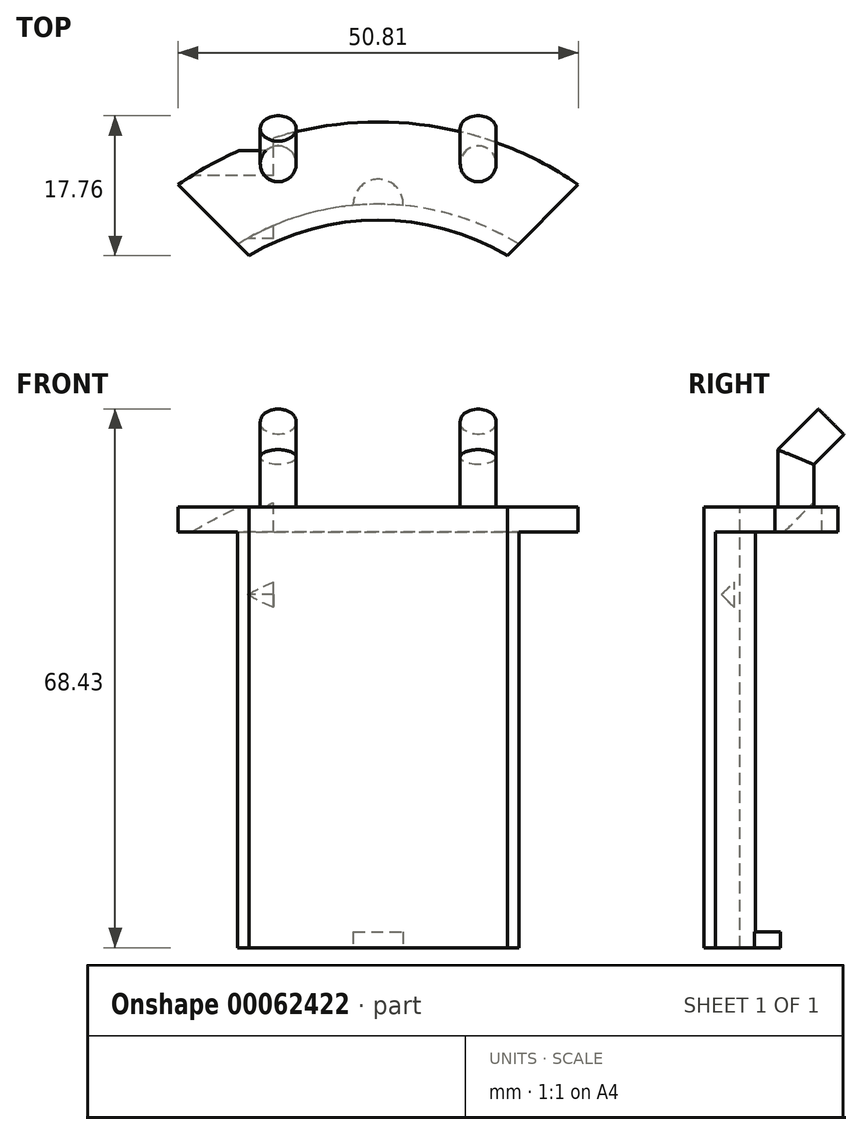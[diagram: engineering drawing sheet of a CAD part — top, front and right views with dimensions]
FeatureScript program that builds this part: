
annotation { "Feature Type Name" : "Feature", "Feature Type Description" : "" }
export const myFeature = defineFeature(function(context is Context, id is Id, definition is map)
    precondition{}
    {
        {
            var Q0;
            Q0=qCreatedBy(makeId("Top.planeOp"),FACE);
            var sketch = newSketch(context, id + "F0", { "sketchPlane" : qUnion([Q0])});
            skLineSegment(sketch, "E0.bottom", {"start": v(0, 0) * mm, "end": v(31.75, 0) * mm});
            skLineSegment(sketch, "E0.top", {"start": v(0, 9.52) * mm, "end": v(31.75, 9.52) * mm});
            skLineSegment(sketch, "E0.left", {"start": v(0, 0) * mm, "end": v(0, 9.52) * mm});
            skLineSegment(sketch, "E0.right", {"start": v(31.75, 0) * mm, "end": v(31.75, 9.52) * mm});
            skSolve(sketch);
        }
        {
            var Q0;
            Q0=makeQuery(id+"F0.imprint","IMPRINT",FACE,{"disambiguationData":[TD([[makeQuery(id+"F0.imprint","IMPRINT",EDGE,{"derivedFrom":sQuery(id+"F0.wireOp",EDGE,"E0.bottom")}),1.0]])]});
            extrude(context, id + "F1", {"entities" : qUnion([Q0]), "depth" : 3.17 * mm});
        }
        {
            var Q0;
            Q0=makeQuery(id+"F1.opExtrude","SWEPT_FACE",FACE,{"disambiguationData":[OSD([sQuery(id+"F0.wireOp",EDGE,"E0.right")])]});
            cPlane(context, id + "F2", {"entities" : qUnion([Q0]), "cplaneType" : CPlaneType.OFFSET, "offset" : 3.17 * mm, "oppositeDirection" : true, "width" : 152.4 * mm, "height" : 152.4 * mm});
        }
        {
            var Q0;
            Q0=qCreatedBy(id+"F2.planeOp",FACE);
            var sketch = newSketch(context, id + "F3", { "sketchPlane" : qUnion([Q0])});
            skLineSegment(sketch, "E1", {"start": v(7.14, 3.18) * mm, "end": v(7.14, 9.53) * mm});
            skLineSegment(sketch, "E2", {"start": v(7.14, 9.53) * mm, "end": v(11.63, 14.02) * mm});
            skSolve(sketch);
        }
        {
            var Q0;
            Q0=makeQuery(id+"F1.opExtrude","CAP_FACE",FACE,{"disambiguationData":[OSD([sQuery(id+"F0.wireOp",EDGE,"E0.bottom"),sQuery(id+"F0.wireOp",EDGE,"E0.top"),sQuery(id+"F0.wireOp",EDGE,"E0.left"),sQuery(id+"F0.wireOp",EDGE,"E0.right")])],"isStart":false});
            var sketch = newSketch(context, id + "F4", { "sketchPlane" : qUnion([Q0])});
            skCircle(sketch, "E3", {"center": v(28.57, 7.14) * mm, "radius": 2.29 * mm});
            skSolve(sketch);
        }
        {
            var Q0;
            Q0=makeQuery(id+"F4.imprint","IMPRINT",FACE,{"disambiguationData":[TD([[makeQuery(id+"F4.imprint","IMPRINT",EDGE,{"derivedFrom":sQuery(id+"F4.wireOp",EDGE,"E3")}),1.0]])]});
            var Q1;
            Q1=sQuery(id+"F3.wireOp",EDGE,"E1");
            var Q2;
            Q2=sQuery(id+"F3.wireOp",EDGE,"E2");
            sweep(context, id + "F5", {"operationType" : NewBodyOperationType.ADD, "profiles" : qUnion([Q0]), "path" : qUnion([Q1, Q2])});
        }
        {
            var Q0;
            Q0=qCreatedBy(id+"F2.planeOp",FACE);
            cPlane(context, id + "F6", {"entities" : qUnion([Q0]), "cplaneType" : CPlaneType.OFFSET, "offset" : 25.4 * mm, "oppositeDirection" : true, "width" : 152.4 * mm, "height" : 152.4 * mm});
        }
        {
            var Q0;
            Q0=qCreatedBy(id+"F6.planeOp",FACE);
            var sketch = newSketch(context, id + "F7", { "sketchPlane" : qUnion([Q0])});
            skLineSegment(sketch, "E4.0", {"start": v(7.14, 3.18) * mm, "end": v(7.14, 9.53) * mm});
            skLineSegment(sketch, "E4.1", {"start": v(7.14, 9.53) * mm, "end": v(11.63, 14.02) * mm});
            skSolve(sketch);
        }
        {
            var Q0;
            Q0=makeQuery(id+"F1.opExtrude","CAP_FACE",FACE,{"disambiguationData":[OSD([sQuery(id+"F0.wireOp",EDGE,"E0.bottom"),sQuery(id+"F0.wireOp",EDGE,"E0.top"),sQuery(id+"F0.wireOp",EDGE,"E0.left"),sQuery(id+"F0.wireOp",EDGE,"E0.right")])],"isStart":false});
            var sketch = newSketch(context, id + "F8", { "sketchPlane" : qUnion([Q0])});
            skCircle(sketch, "E5", {"center": v(3.17, 7.14) * mm, "radius": 2.29 * mm});
            skSolve(sketch);
        }
        {
            var Q0;
            Q0=makeQuery(id+"F8.imprint","IMPRINT",FACE,{"disambiguationData":[TD([[makeQuery(id+"F8.imprint","IMPRINT",EDGE,{"derivedFrom":sQuery(id+"F8.wireOp",EDGE,"E5")}),1.0]])]});
            var Q1;
            Q1=sQuery(id+"F7.wireOp",EDGE,"E4.0");
            var Q2;
            Q2=sQuery(id+"F7.wireOp",EDGE,"E4.1");
            sweep(context, id + "F9", {"operationType" : NewBodyOperationType.ADD, "profiles" : qUnion([Q0]), "path" : qUnion([Q1, Q2])});
        }
        {
            var Q0;
            Q0=makeQuery(id+"F1.opExtrude","CAP_FACE",FACE,{"disambiguationData":[OSD([sQuery(id+"F0.wireOp",EDGE,"E0.bottom"),sQuery(id+"F0.wireOp",EDGE,"E0.top"),sQuery(id+"F0.wireOp",EDGE,"E0.left"),sQuery(id+"F0.wireOp",EDGE,"E0.right")])],"isStart":false});
            var sketch = newSketch(context, id + "F10", { "sketchPlane" : qUnion([Q0])});
            skArc(sketch, "E6", {"start": v(41.28, 4.48) * mm, "mid": v(15.88, 12.46) * mm, "end": v(-9.52, 4.48) * mm});
            skArc(sketch, "E7", {"start": v(32.27, -4.52) * mm, "mid": v(15.88, 0) * mm, "end": v(-0.52, -4.52) * mm});
            skLineSegment(sketch, "E8", {"start": v(-9.53, 4.48) * mm, "end": v(-0.52, -4.52) * mm});
            skLineSegment(sketch, "E9", {"start": v(32.27, -4.52) * mm, "end": v(41.27, 4.48) * mm});
            skSolve(sketch);
        }
        {
            var Q0;
            Q0 = qSketchRegion(id + "F10", true);
            var Q1;
            Q1=makeQuery(id+"F1.opExtrude","CAP_FACE",FACE,{"disambiguationData":[OSD([sQuery(id+"F0.wireOp",EDGE,"E0.bottom"),sQuery(id+"F0.wireOp",EDGE,"E0.top"),sQuery(id+"F0.wireOp",EDGE,"E0.left"),sQuery(id+"F0.wireOp",EDGE,"E0.right")])],"isStart":true});
            extrude(context, id + "F11", {"entities" : qUnion([Q0]), "operationType" : NewBodyOperationType.ADD, "endBound" : BoundingType.UP_TO_SURFACE, "oppositeDirection" : true, "endBoundEntityFace" : qUnion([Q1]), "depth" : 25.4 * mm});
        }
        {
            var Q0;
            {var subQ0=sQuery(id+"F0.wireOp",EDGE,"E0.right");var subQ1=sQuery(id+"F0.wireOp",EDGE,"E0.left");var subQ2=sQuery(id+"F0.wireOp",EDGE,"E0.top");var subQ3=sQuery(id+"F0.wireOp",EDGE,"E0.bottom");Q0=makeQuery(id+"F11.boolean.opBoolean","MERGE",FACE,{"derivedFrom":[makeQuery(id+"F1.opExtrude","CAP_FACE",FACE,{"disambiguationData":[OSD([subQ3,subQ2,subQ1,subQ0])],"isStart":true}),makeQuery(id+"F11.opExtrude","CAP_FACE",FACE,{"disambiguationData":[OSD([subQ3,subQ2,subQ1,subQ0])],"isStart":false})]});}
            var sketch = newSketch(context, id + "F12", { "sketchPlane" : qUnion([Q0])});
            skArc(sketch, "E10.0", {"start": v(-1.98, 3.06) * mm, "mid": v(15.87, -2) * mm, "end": v(33.73, 3.06) * mm});
            skArc(sketch, "E11.0", {"start": v(-0.52, 4.52) * mm, "mid": v(15.88, 0) * mm, "end": v(32.27, 4.52) * mm});
            skLineSegment(sketch, "E12", {"start": v(-1.98, 3.06) * mm, "end": v(-0.52, 4.52) * mm});
            skLineSegment(sketch, "E13", {"start": v(33.73, 3.06) * mm, "end": v(32.27, 4.52) * mm});
            skSolve(sketch);
        }
        {
            var Q0;
            Q0 = qSketchRegion(id + "F12", true);
            extrude(context, id + "F13", {"entities" : qUnion([Q0]), "operationType" : NewBodyOperationType.ADD, "depth" : 52.8 * mm});
        }
        {
            var Q0;
            Q0=makeQuery(id+"F9.opSweep","CAP_FACE",FACE,{"disambiguationData":[OSD([sQuery(id+"F7.wireOp",VERTEX,"E4.1.end"),sQuery(id+"F8.wireOp",EDGE,"E5")])],"isStart":false});
            var sketch = newSketch(context, id + "F14", { "sketchPlane" : qUnion([Q0])});
            skLineSegment(sketch, "E14.bottom", {"start": v(-2.6, -3.97) * mm, "end": v(34.35, -3.97) * mm});
            skLineSegment(sketch, "E14.top", {"start": v(-2.6, -10.25) * mm, "end": v(34.35, -10.25) * mm});
            skLineSegment(sketch, "E14.left", {"start": v(-2.6, -3.97) * mm, "end": v(-2.6, -10.25) * mm});
            skLineSegment(sketch, "E14.right", {"start": v(34.35, -3.97) * mm, "end": v(34.35, -10.25) * mm});
            skSolve(sketch);
        }
        {
            var Q0;
            Q0=makeQuery(id+"F14.imprint","IMPRINT",FACE,{"disambiguationData":[TD([[makeQuery(id+"F14.imprint","IMPRINT",EDGE,{"derivedFrom":sQuery(id+"F14.wireOp",EDGE,"E14.top")}),1.0]])]});
            extrude(context, id + "F15", {"entities" : qUnion([Q0]), "operationType" : NewBodyOperationType.REMOVE, "oppositeDirection" : true, "depth" : 25.4 * mm});
        }
        {
            var Q0;
            Q0=makeQuery(id+"F13.opExtrude","CAP_FACE",FACE,{"disambiguationData":[OSD([sQuery(id+"F12.wireOp",EDGE,"E10.0"),sQuery(id+"F12.wireOp",EDGE,"E11.0"),sQuery(id+"F12.wireOp",EDGE,"E12"),sQuery(id+"F12.wireOp",EDGE,"E13")])],"isStart":false});
            var sketch = newSketch(context, id + "F16", { "sketchPlane" : qUnion([Q0])});
            skArc(sketch, "E15", {"start": v(12.7, -1.85) * mm, "mid": v(15.88, -5.18) * mm, "end": v(19.05, -1.85) * mm});
            skArc(sketch, "E16", {"start": v(12.7, -1.85) * mm, "mid": v(15.88, -2) * mm, "end": v(19.05, -1.85) * mm});
            skSolve(sketch);
        }
        {
            var Q0;
            Q0=makeQuery(id+"F16.imprint","IMPRINT",FACE,{"disambiguationData":[TD([[makeQuery(id+"F16.imprint","IMPRINT",EDGE,{"derivedFrom":sQuery(id+"F16.wireOp",EDGE,"E15")}),1.0]])]});
            extrude(context, id + "F17", {"entities" : qUnion([Q0]), "operationType" : NewBodyOperationType.ADD, "oppositeDirection" : true, "depth" : 2 * mm});
        }
    });
